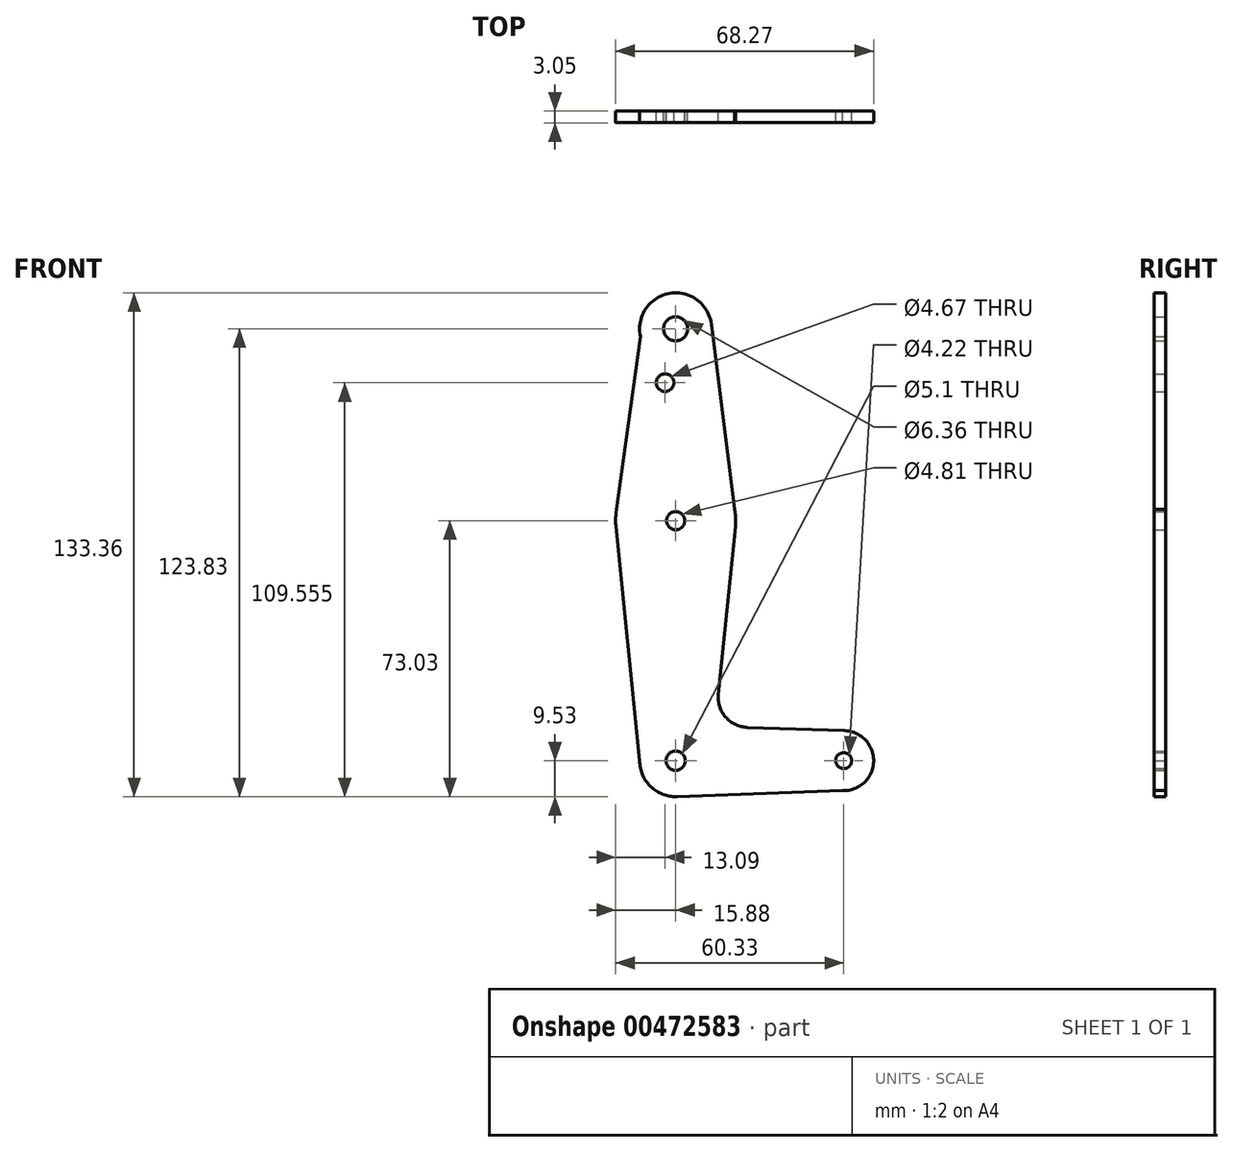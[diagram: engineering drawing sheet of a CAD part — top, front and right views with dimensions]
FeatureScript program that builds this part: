
annotation { "Feature Type Name" : "Feature", "Feature Type Description" : "" }
export const myFeature = defineFeature(function(context is Context, id is Id, definition is map)
    precondition{}
    {
        {
            var Q0;
            Q0=qCreatedBy(makeId("Front.planeOp"),FACE);
            var sketch = newSketch(context, id + "F0", { "sketchPlane" : qUnion([Q0])});
            skLineSegment(sketch, "E0", {"start": v(0, 114.3) * mm, "end": v(0, 0) * mm, "construction": true});
            skLineSegment(sketch, "E1", {"start": v(0, 0) * mm, "end": v(44.45, 0) * mm, "construction": true});
            skCircle(sketch, "E2", {"center": v(0, 114.3) * mm, "radius": 9.53 * mm});
            skCircle(sketch, "E3", {"center": v(0, 63.5) * mm, "radius": 15.88 * mm});
            skCircle(sketch, "E4", {"center": v(0, 0) * mm, "radius": 9.53 * mm});
            skCircle(sketch, "E5", {"center": v(44.45, 0) * mm, "radius": 7.94 * mm});
            skLineSegment(sketch, "E6", {"start": v(44.13, -7.93) * mm, "end": v(0, -9.53) * mm});
            skLineSegment(sketch, "E7", {"start": v(44.72, 7.93) * mm, "end": v(18.94, 8.8) * mm});
            skLineSegment(sketch, "E8", {"start": v(-9.31, 112.3) * mm, "end": v(-15.73, 65.66) * mm});
            skLineSegment(sketch, "E9", {"start": v(15.57, 66.6) * mm, "end": v(9.45, 115.48) * mm});
            skLineSegment(sketch, "E10", {"start": v(9.45, 115.48) * mm, "end": v(8.76, 112.98) * mm});
            skLineSegment(sketch, "E11", {"start": v(-9.53, 0) * mm, "end": v(-15.8, 61.9) * mm});
            skLineSegment(sketch, "E12", {"start": v(11.3, 17.56) * mm, "end": v(15.8, 61.9) * mm});
            skCircle(sketch, "E13", {"center": v(0, 114.3) * mm, "radius": 3.18 * mm});
            skCircle(sketch, "E14", {"center": v(-2.8, 100.03) * mm, "radius": 2.34 * mm});
            skCircle(sketch, "E15", {"center": v(0, 63.5) * mm, "radius": 2.4 * mm});
            skCircle(sketch, "E16", {"center": v(0, 0) * mm, "radius": 2.55 * mm});
            skCircle(sketch, "E17", {"center": v(44.45, 0) * mm, "radius": 2.1 * mm});
            skPoint(sketch, "E18.newPointB", {"position": v(0, 9.45) * mm});
            skArc(sketch, "E18.filletArc", {"start": v(11.3, 17.56) * mm, "mid": v(13.22, 11.53) * mm, "end": v(18.94, 8.8) * mm});
            skSolve(sketch);
        }
        {
            var Q0;
            Q0 = qSketchRegion(id + "F0", true);
            extrude(context, id + "F1", {"entities" : qUnion([Q0]), "depth" : 3.05 * mm});
        }
    });
